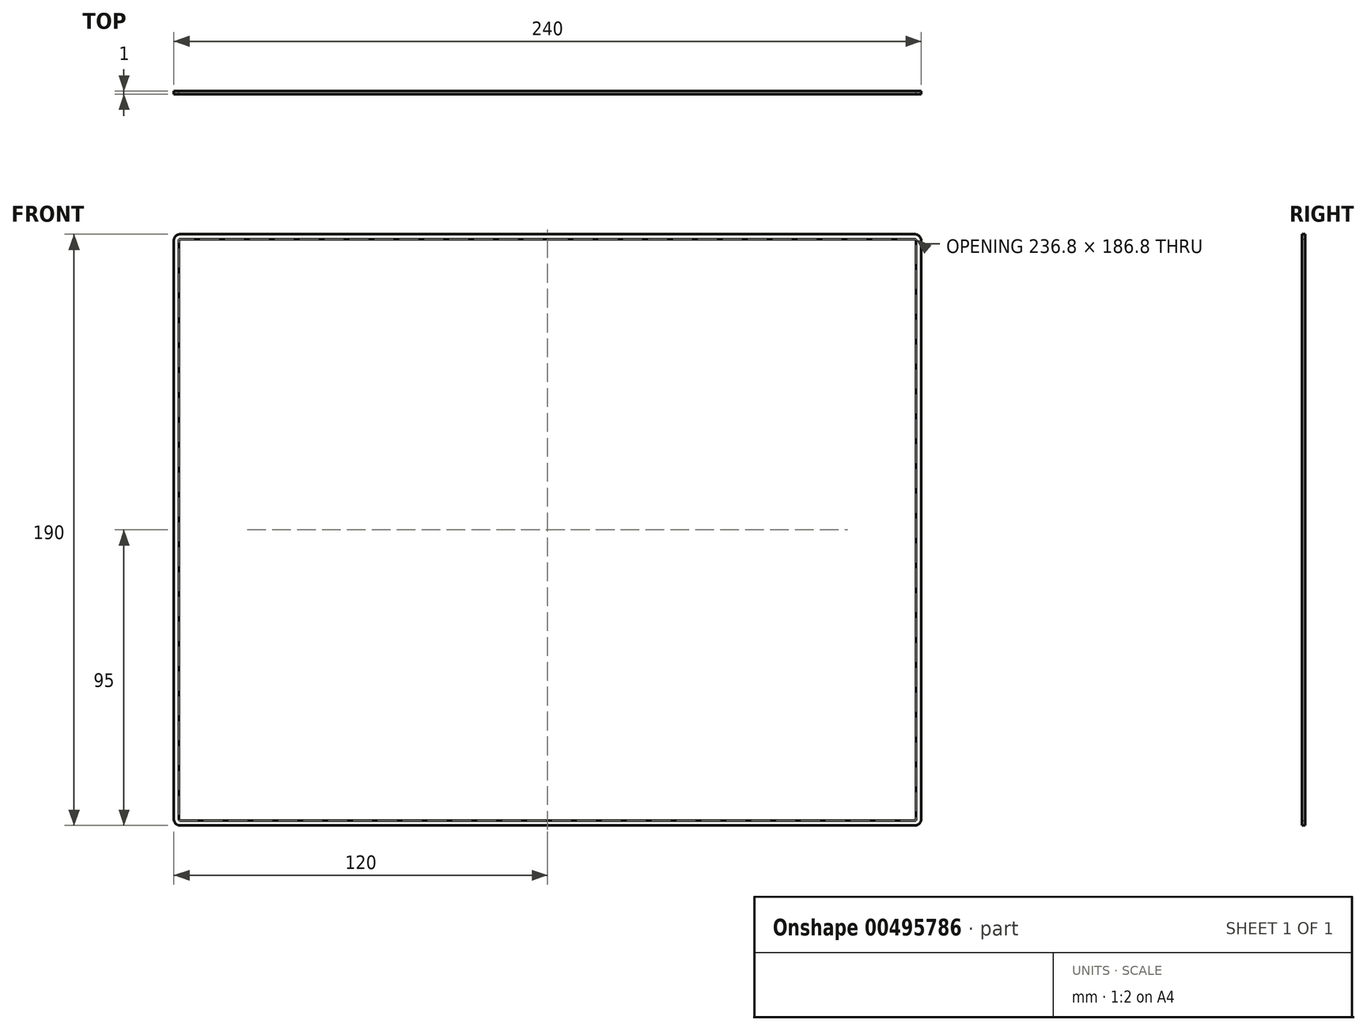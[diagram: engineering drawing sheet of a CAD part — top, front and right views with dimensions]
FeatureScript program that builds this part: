
annotation { "Feature Type Name" : "Feature", "Feature Type Description" : "" }
export const myFeature = defineFeature(function(context is Context, id is Id, definition is map)
    precondition{}
    {
        {
            var Q0;
            Q0=qCreatedBy(makeId("Front.planeOp"),FACE);
            var sketch = newSketch(context, id + "F0", { "sketchPlane" : qUnion([Q0])});
            skLineSegment(sketch, "E0.bottom", {"start": v(120, -95) * mm, "end": v(-120, -95) * mm});
            skLineSegment(sketch, "E0.top", {"start": v(120, 95) * mm, "end": v(-120, 95) * mm});
            skLineSegment(sketch, "E0.left", {"start": v(120, -95) * mm, "end": v(120, 95) * mm});
            skLineSegment(sketch, "E0.right", {"start": v(-120, -95) * mm, "end": v(-120, 95) * mm});
            skPoint(sketch, "E0.middle", {"position": v(0, 0) * mm});
            skSolve(sketch);
        }
        {
            var Q0;
            Q0=makeQuery(id+"F0.imprint","IMPRINT",FACE,{"disambiguationData":[TD([[makeQuery(id+"F0.imprint","IMPRINT",EDGE,{"derivedFrom":sQuery(id+"F0.wireOp",EDGE,"E0.bottom")}),-1.0]])]});
            extrude(context, id + "F1", {"entities" : qUnion([Q0]), "depth" : 1 * mm});
        }
        {
            var Q0;
            Q0=makeQuery(id+"F1.opExtrude","SWEPT_EDGE",EDGE,{"disambiguationData":[OSD([sQuery(id+"F0.wireOp",EDGE,"E0.top"),sQuery(id+"F0.wireOp",EDGE,"E0.left")])]});
            var Q1;
            Q1=makeQuery(id+"F1.opExtrude","SWEPT_EDGE",EDGE,{"disambiguationData":[OSD([sQuery(id+"F0.wireOp",EDGE,"E0.top"),sQuery(id+"F0.wireOp",EDGE,"E0.right")])]});
            var Q2;
            Q2=makeQuery(id+"F1.opExtrude","SWEPT_EDGE",EDGE,{"disambiguationData":[OSD([sQuery(id+"F0.wireOp",EDGE,"E0.bottom"),sQuery(id+"F0.wireOp",EDGE,"E0.right")])]});
            var Q3;
            Q3=makeQuery(id+"F1.opExtrude","SWEPT_EDGE",EDGE,{"disambiguationData":[OSD([sQuery(id+"F0.wireOp",EDGE,"E0.bottom"),sQuery(id+"F0.wireOp",EDGE,"E0.left")])]});
            fillet(context, id + "F2", {"entities" : qUnion([Q0, Q1, Q2, Q3]), "radius" : 2 * mm, "tangentPropagation" : true, "allowEdgeOverflow" : false});
        }
        {
            var Q0;
            Q0=makeQuery(id+"F1.opExtrude","CAP_FACE",FACE,{"disambiguationData":[OSD([sQuery(id+"F0.wireOp",EDGE,"E0.bottom"),sQuery(id+"F0.wireOp",EDGE,"E0.top"),sQuery(id+"F0.wireOp",EDGE,"E0.left"),sQuery(id+"F0.wireOp",EDGE,"E0.right")])],"isStart":true});
            var Q1;
            Q1=makeQuery(id+"F1.opExtrude","CAP_FACE",FACE,{"disambiguationData":[OSD([sQuery(id+"F0.wireOp",EDGE,"E0.bottom"),sQuery(id+"F0.wireOp",EDGE,"E0.top"),sQuery(id+"F0.wireOp",EDGE,"E0.left"),sQuery(id+"F0.wireOp",EDGE,"E0.right")])],"isStart":false});
            var Q2;
            Q2=makeQuery(id+"F1.opExtrude","SWEPT_BODY",BODY,{"disambiguationData":[OSD([sQuery(id+"F0.wireOp",EDGE,"E0.bottom"),sQuery(id+"F0.wireOp",EDGE,"E0.top"),sQuery(id+"F0.wireOp",EDGE,"E0.left"),sQuery(id+"F0.wireOp",EDGE,"E0.right")])]});
            shell(context, id + "F3", {"entities" : qUnion([Q0, Q1]), "parts" : qUnion([Q2]), "thickness" : 1.6 * mm});
        }
    });
